# Revit family: Faucet-Deck_Mount-Bath-KOHLER-AVID-K-97363T_1
name_source: partatom
category: Plumbing Fixtures
revit_build: Autodesk Revit 2017 (Build: 20160225_1515(x64)
units: mm (PartAtom-declared; Revit-internal decimal feet)

## family parameters
Cut with Voids When Loaded = No
Host = Face
OmniClass Number = 23.31.11.00
OmniClass Title = Faucets
Part Type = Normal
Room Calculation Point = No
Round Connector Dimension = Use Diameter
Shared = No

## types (4) — shared parameters
ADA Compliant = No
Assembly Code = D2010
CW Connection = Yes
Cold Water Inlet = Cold Water Inlet
Date Modified = 06/10/2020
Default Elevation = 36"
Drain Included = No
HW Connection = Yes
Handle Clearance = 4 1/8"
Height = 6 7/8"
Hot Water Inlet = Hot Water Inlet
Length = 7 13/16"
Manufacturer = KOHLER Co.
Master Format 2014 = 22 41 39
Master Format 2014 Name = Residential Faucets, Supplies, and Trim
Material = Premium Metal Construction
Product Name = AVID
Spout Reach = 7 13/16"
URL = http://www.kohler.com.cn
Vent Connection = No
Waste Connection = No
Waste Water Outlet = Waste Water Outlet
WaterSense Certified = No

## per-type parameters (varying)
| type | Description | Finish | Flow Rate | Model | Pressure | Product Page URL | Type |
| 9.25 GPM, CP-Polished Chrome | Cylinder side double handle bathtub faucet | Kohler-Metal-CP-Polished_Chrome | 9 GPM | K-97363T-4-CP | 60.00 psi | http://www.kohler.com.cn | 1 |
| 9.25 GPM, TT-Titanium Silver | Cylinder side double handle bathtub faucet | Kohler-Metal-TT-Titanium_Silver | 9 GPM | K-97363T-4-TT | 60.00 psi | http://www.kohler.com.cn | 2 |
| 12 GPM, CP-Polished Chrome | Two handle deckmount bath faucet | Kohler-Metal-CP-Polished_Chrome | 12 GPM | K-97363T-4E-CP | 45.00 psi |  | 3 |
| 12 GPM, TT-Titanium Silver | Two handle deckmount bath faucet | Kohler-Metal-TT-Titanium_Silver | 12 GPM | K-97363T-4E-TT | 45.00 psi |  | 4 |

## geometry (parser evidence)
native form markers: Sweep x9
no freeform markers — native parametric forms only
